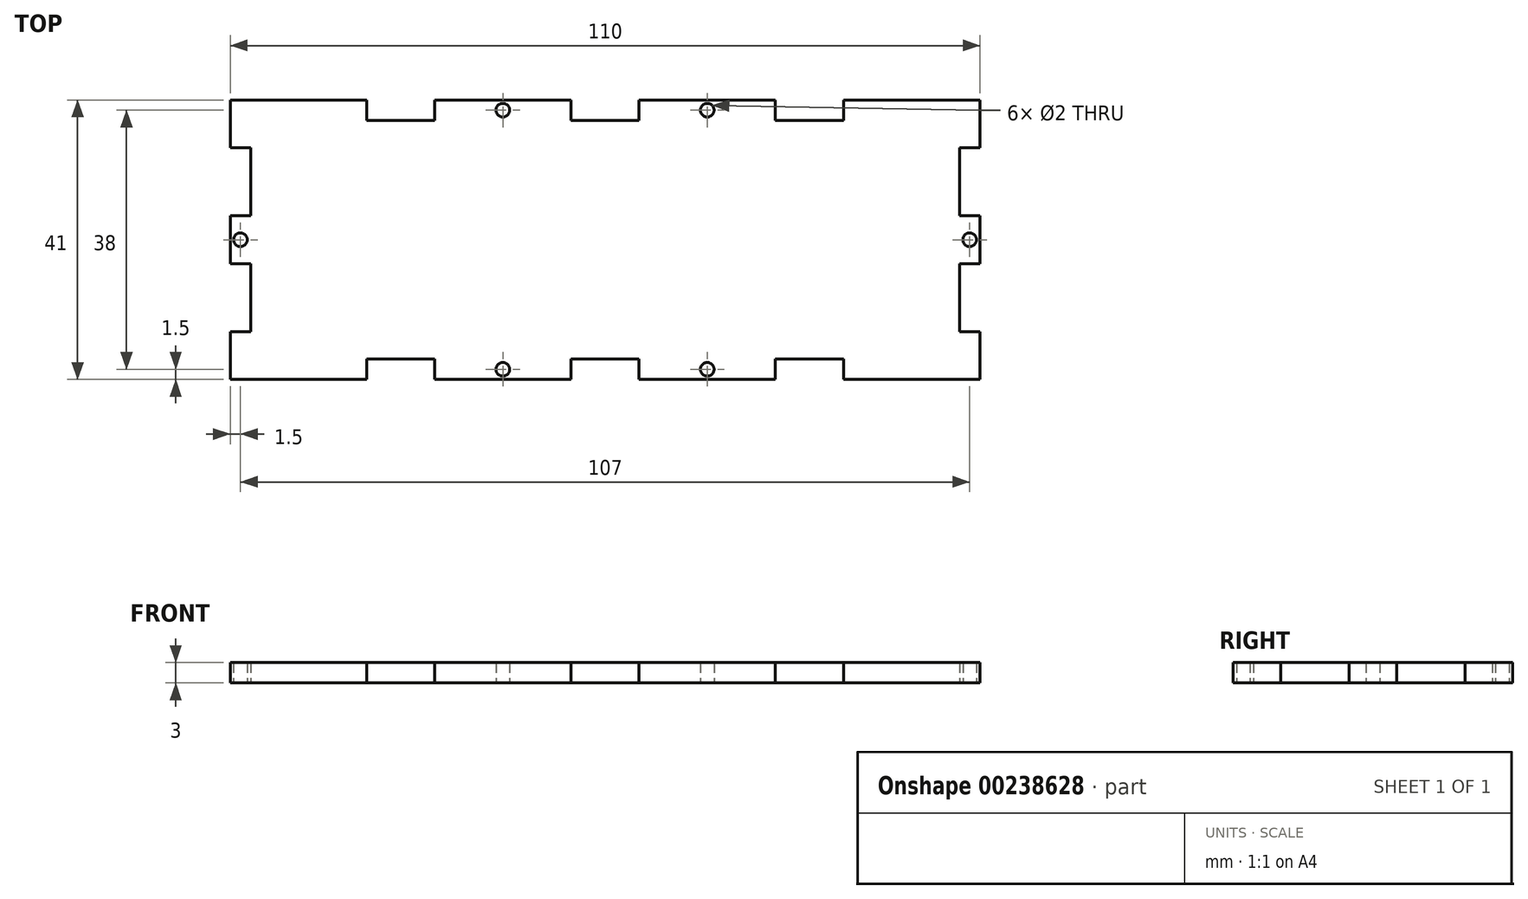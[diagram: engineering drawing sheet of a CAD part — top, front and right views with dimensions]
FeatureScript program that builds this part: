
annotation { "Feature Type Name" : "Feature", "Feature Type Description" : "" }
export const myFeature = defineFeature(function(context is Context, id is Id, definition is map)
    precondition{}
    {
        {
            var Q0;
            Q0=qCreatedBy(makeId("Top.planeOp"),FACE);
            var sketch = newSketch(context, id + "F0", { "sketchPlane" : qUnion([Q0])});
            skLineSegment(sketch, "E0.bottom", {"start": v(55, 20.5) * mm, "end": v(35, 20.5) * mm});
            skLineSegment(sketch, "E0.top", {"start": v(55, -20.5) * mm, "end": v(35, -20.5) * mm});
            skLineSegment(sketch, "E0.left", {"start": v(55, 20.5) * mm, "end": v(55, 13.5) * mm});
            skLineSegment(sketch, "E0.right", {"start": v(-55, 20.5) * mm, "end": v(-55, 13.5) * mm});
            skLineSegment(sketch, "E1.trimOffspring", {"start": v(-55, 3.5) * mm, "end": v(-55, -3.5) * mm});
            skLineSegment(sketch, "E2.trimOffspring", {"start": v(-35, 20.5) * mm, "end": v(-55, 20.5) * mm});
            skLineSegment(sketch, "E3.trimOffspring", {"start": v(-35, -20.5) * mm, "end": v(-55, -20.5) * mm});
            skLineSegment(sketch, "E4.trimOffspring", {"start": v(55, 3.5) * mm, "end": v(55, -3.5) * mm});
            skLineSegment(sketch, "E5.trimOffspring", {"start": v(55, -13.5) * mm, "end": v(55, -20.5) * mm});
            skLineSegment(sketch, "E6.trimOffspring", {"start": v(-55, -13.5) * mm, "end": v(-55, -20.5) * mm});
            skLineSegment(sketch, "E7", {"start": v(-25, -20.5) * mm, "end": v(-5, -20.5) * mm});
            skLineSegment(sketch, "E8", {"start": v(5, -20.5) * mm, "end": v(25, -20.5) * mm});
            skLineSegment(sketch, "E9", {"start": v(25, 20.5) * mm, "end": v(5, 20.5) * mm});
            skLineSegment(sketch, "E10", {"start": v(-25, 20.5) * mm, "end": v(-5, 20.5) * mm});
            skLineSegment(sketch, "E11", {"start": v(-35, 20.5) * mm, "end": v(-35, 17.5) * mm});
            skLineSegment(sketch, "E12", {"start": v(-35, 17.5) * mm, "end": v(-25, 17.5) * mm});
            skLineSegment(sketch, "E13", {"start": v(-25, 17.5) * mm, "end": v(-25, 20.5) * mm});
            skLineSegment(sketch, "E14", {"start": v(-5, 20.5) * mm, "end": v(-5, 17.5) * mm});
            skLineSegment(sketch, "E15", {"start": v(-5, 17.5) * mm, "end": v(5, 17.5) * mm});
            skLineSegment(sketch, "E16", {"start": v(5, 17.5) * mm, "end": v(5, 20.5) * mm});
            skLineSegment(sketch, "E17", {"start": v(25, 20.5) * mm, "end": v(25, 17.5) * mm});
            skLineSegment(sketch, "E18", {"start": v(25, 17.5) * mm, "end": v(35, 17.5) * mm});
            skLineSegment(sketch, "E19", {"start": v(35, 17.5) * mm, "end": v(35, 20.5) * mm});
            skLineSegment(sketch, "E20", {"start": v(-35, -20.5) * mm, "end": v(-35, -17.5) * mm});
            skLineSegment(sketch, "E21", {"start": v(-25, -17.5) * mm, "end": v(-25, -20.5) * mm});
            skLineSegment(sketch, "E22", {"start": v(25, -20.5) * mm, "end": v(25, -17.5) * mm});
            skLineSegment(sketch, "E23", {"start": v(25, -17.5) * mm, "end": v(35, -17.5) * mm});
            skLineSegment(sketch, "E24", {"start": v(35, -17.5) * mm, "end": v(35, -20.5) * mm});
            skLineSegment(sketch, "E25", {"start": v(-5, -20.5) * mm, "end": v(-5, -17.5) * mm});
            skLineSegment(sketch, "E26", {"start": v(-5, -17.5) * mm, "end": v(5, -17.5) * mm});
            skLineSegment(sketch, "E27", {"start": v(5, -17.5) * mm, "end": v(5, -20.5) * mm});
            skLineSegment(sketch, "E28", {"start": v(-35, -17.5) * mm, "end": v(-25, -17.5) * mm});
            skLineSegment(sketch, "E29", {"start": v(55, 13.5) * mm, "end": v(52, 13.5) * mm});
            skLineSegment(sketch, "E30", {"start": v(52, 13.5) * mm, "end": v(52, 3.5) * mm});
            skLineSegment(sketch, "E31", {"start": v(52, 3.5) * mm, "end": v(55, 3.5) * mm});
            skLineSegment(sketch, "E32", {"start": v(55, -3.5) * mm, "end": v(52, -3.5) * mm});
            skLineSegment(sketch, "E33", {"start": v(52, -3.5) * mm, "end": v(52, -13.5) * mm});
            skLineSegment(sketch, "E34", {"start": v(52, -13.5) * mm, "end": v(55, -13.5) * mm});
            skLineSegment(sketch, "E35", {"start": v(-55, 13.5) * mm, "end": v(-52, 13.5) * mm});
            skLineSegment(sketch, "E36", {"start": v(-52, 13.5) * mm, "end": v(-52, 3.5) * mm});
            skLineSegment(sketch, "E37", {"start": v(-52, 3.5) * mm, "end": v(-55, 3.5) * mm});
            skLineSegment(sketch, "E38", {"start": v(-55, -3.5) * mm, "end": v(-52, -3.5) * mm});
            skLineSegment(sketch, "E39", {"start": v(-52, -3.5) * mm, "end": v(-52, -13.5) * mm});
            skLineSegment(sketch, "E40", {"start": v(-52, -13.5) * mm, "end": v(-55, -13.5) * mm});
            skCircle(sketch, "E41", {"center": v(-15, 19) * mm, "radius": 1 * mm});
            skPoint(sketch, "E41.centerSnap0", {"position": v(-25, 19) * mm});
            skPoint(sketch, "E41.centerSnap1", {"position": v(-15, 20.5) * mm});
            skPoint(sketch, "E41.perimeterSnap0", {"position": v(-25, 19) * mm});
            skCircle(sketch, "E42", {"center": v(15, 19) * mm, "radius": 1 * mm});
            skPoint(sketch, "E42.centerSnap0", {"position": v(15, 20.5) * mm});
            skPoint(sketch, "E42.centerSnap1", {"position": v(5, 19) * mm});
            skCircle(sketch, "E43", {"center": v(-53.5, 0) * mm, "radius": 1 * mm});
            skPoint(sketch, "E43.centerSnap0", {"position": v(-53.5, 3.5) * mm});
            skPoint(sketch, "E43.centerSnap1", {"position": v(-55, 0) * mm});
            skCircle(sketch, "E44", {"center": v(-15, -19) * mm, "radius": 1 * mm});
            skPoint(sketch, "E44.centerSnap0", {"position": v(-25, -19) * mm});
            skPoint(sketch, "E44.centerSnap1", {"position": v(-15, -20.5) * mm});
            skCircle(sketch, "E45", {"center": v(15, -19) * mm, "radius": 1 * mm});
            skPoint(sketch, "E45.centerSnap0", {"position": v(15, -20.5) * mm});
            skPoint(sketch, "E45.centerSnap1", {"position": v(25, -19) * mm});
            skCircle(sketch, "E46", {"center": v(53.5, 0) * mm, "radius": 1 * mm});
            skPoint(sketch, "E46.centerSnap0", {"position": v(55, 0) * mm});
            skPoint(sketch, "E46.centerSnap1", {"position": v(53.5, 3.5) * mm});
            skSolve(sketch);
        }
        {
            var Q0;
            Q0=qSketchRegion(id+"F0",true);
            extrude(context, id + "F1", {"entities" : qUnion([Q0]), "depth" : 3 * mm, "offsetDistance" : 25 * mm});
        }
    });
